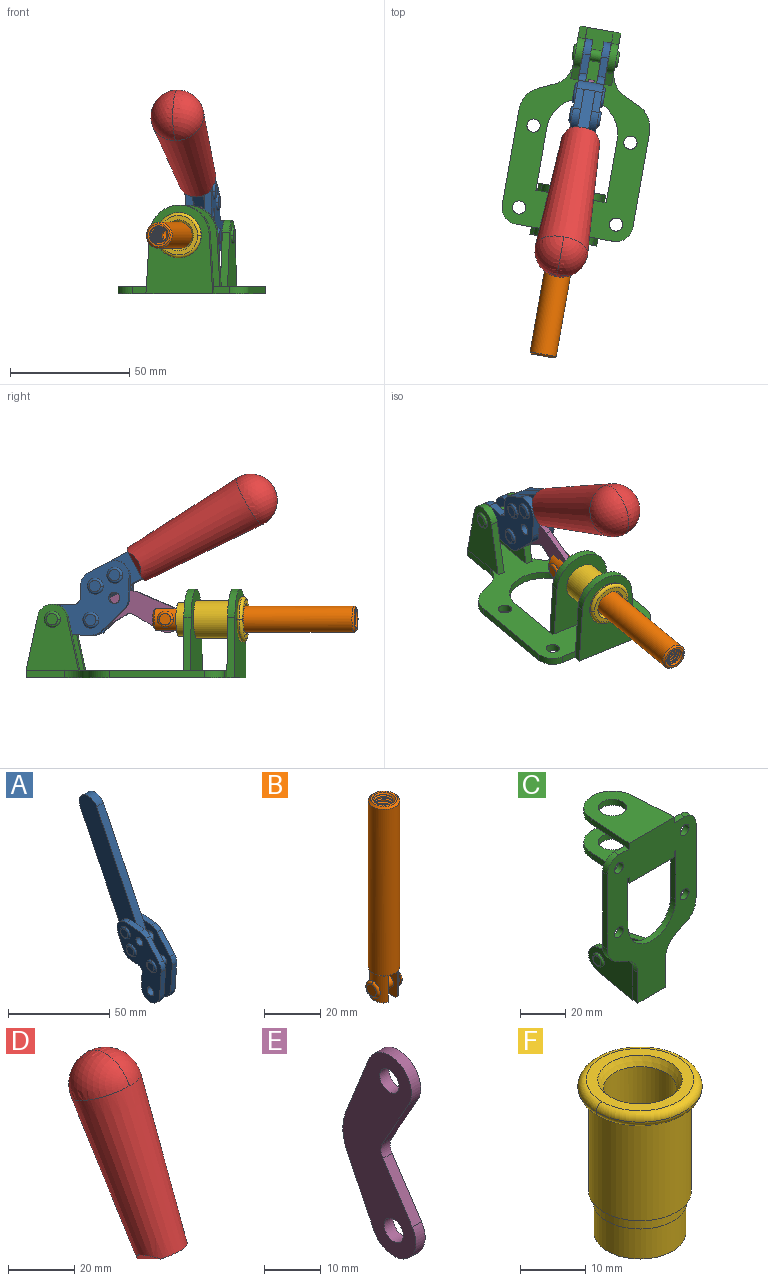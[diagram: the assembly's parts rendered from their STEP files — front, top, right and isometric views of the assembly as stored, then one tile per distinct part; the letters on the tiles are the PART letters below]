
ASSEMBLY  parts=6 mates=6
PART A: 59 faces, bbox 12.9x60.2x99.6 mm
  f0: torus R=2.39mm, axis (-1,0,0), area 14.9mm2, adj f20,f43,f51
  f1: torus R=2.39mm, axis (-1,0,0), area 14.9mm2, adj f19,f42,f51
  f2: torus R=2.39mm, axis (-1,0,0), area 14.9mm2, adj f18,f35,f51
  f3: torus R=2.39mm, axis (-1,0,0), area 14.9mm2, adj f14,f17,f23
  f4: torus R=2.39mm, axis (-1,0,0), area 14.9mm2, adj f13,f16,f23
  f5: torus R=2.39mm, axis (-1,0,0), area 14.9mm2, adj f12,f15,f23
  f6: cylinder r=2.39mm len=4.78mm, axis (1,0,0), area 46.5mm2, adj f48,f50,f51
  f7: cylinder r=2.39mm len=4.78mm, axis (1,0,0), area 46.5mm2, adj f50,f51
  f8: cylinder r=6.35mm len=12.68mm, axis (1,0,0), area 61.8mm2, adj f38,f39,f50,f51
  f9: cylinder r=2.39mm len=4.78mm, axis (-1,0,0), area 70.5mm2, adj f46,f50
  f10: cylinder r=2.39mm len=4.78mm, axis (-1,0,0), area 46.5mm2, adj f23,f45,f46
  f11: cylinder r=2.39mm len=4.78mm, axis (-1,0,0), area 46.5mm2, adj f23,f46
  f12: plane 4.78x4.78mm, normal (1,0,0), area 17.9mm2, adj f5,f15
  f13: plane 4.78x4.78mm, normal (1,0,0), area 17.9mm2, adj f4,f16
  f14: plane 4.78x4.78mm, normal (1,0,0), area 17.9mm2, adj f3,f17
  f15: torus R=2.39mm, axis (-1,0,0), area 14.9mm2, adj f5,f12,f23
  f16: torus R=2.39mm, axis (-1,0,0), area 14.9mm2, adj f4,f13,f23
  f17: torus R=2.39mm, axis (-1,0,0), area 14.9mm2, adj f3,f14,f23
  f18: plane 4.78x4.78mm, normal (-1,0,0), area 17.9mm2, adj f2,f35
  f19: plane 4.78x4.78mm, normal (-1,0,0), area 17.9mm2, adj f1,f42
  f20: plane 4.78x4.78mm, normal (-1,0,0), area 17.9mm2, adj f0,f43
  f21: plane 2.26x0.2mm, normal (1,0,0), area 0.2mm2, adj f31,f44
  f22: plane 2.26x0.2mm, normal (-1,0,0), area 0.2mm2, adj f41,f44
  f23: plane 39.37x30.77mm, normal (1,0,0), area 565.5mm2, adj f3,f4,f5,f10,f11,f15,f16,f17
  f24: cylinder r=6.1mm len=4.15mm, axis (-1,0,0), area 14.7mm2, adj f23,f25,f32,f46
  f25: plane 10.25x9.01mm, normal (0,-0.75,0.66), area 42.3mm2, adj f23,f24,f26,f46
  f26: cylinder r=6.35mm len=4.64mm, axis (-1,0,0), area 15.6mm2, adj f23,f25,f27,f46
  f27: plane 15.84x3.1mm, normal (0,-1,-0.07), area 49.2mm2, adj f23,f26,f28,f46
  f28: cylinder r=6.35mm len=12.68mm, axis (-1,0,0), area 61.8mm2, adj f23,f27,f29,f46
  f29: plane 8.11x3.1mm, normal (0,1,0.07), area 25.2mm2, adj f23,f28,f30,f46
  f30: cylinder r=3.05mm len=3.25mm, axis (-1,0,0), area 14.8mm2, adj f23,f29,f31,f46
  f31: plane 5.99x3.1mm, normal (0,0.07,-1), area 18.6mm2, adj f21,f23,f30,f44,f46
  f32: plane 9.5x3.1mm, normal (0,-0.07,1), area 29.5mm2, adj f23,f24,f33,f46,f47
  f33: cylinder r=6.1mm len=8.63mm, axis (-1,0,0), area 39.1mm2, adj f23,f32,f34,f47
  f34: plane 8.65x3.96mm, normal (0,0.91,-0.42), area 29.5mm2, adj f23,f33,f44,f47
  f35: torus R=2.39mm, axis (-1,0,0), area 14.9mm2, adj f2,f18,f51
  f36: plane 10.25x9.01mm, normal (0,-0.75,0.66), area 42.3mm2, adj f37,f49,f50,f51
  f37: cylinder r=6.35mm len=4.64mm, axis (1,0,0), area 15.6mm2, adj f36,f38,f50,f51
  f38: plane 15.84x3.1mm, normal (0,-1,-0.07), area 49.2mm2, adj f8,f37,f50,f51
  f39: plane 8.11x3.1mm, normal (0,1,0.07), area 25.2mm2, adj f8,f40,f50,f51
  f40: cylinder r=3.05mm len=3.25mm, axis (1,0,0), area 14.8mm2, adj f39,f41,f50,f51
  f41: plane 5.99x3.1mm, normal (0,0.07,-1), area 18.6mm2, adj f22,f40,f44,f50,f51
  f42: torus R=2.39mm, axis (-1,0,0), area 14.9mm2, adj f1,f19,f51
  f43: torus R=2.39mm, axis (-1,0,0), area 14.9mm2, adj f0,f20,f51
  f44: cylinder r=6.35mm len=12.12mm, axis (-1,0,0), area 128.9mm2, adj f21,f22,f23,f31,f34,f41,f46,f47
  f45: plane 2.65x1.35mm, normal (1,0,0), area 1mm2, adj f10,f55
  f46: plane 39.08x20.42mm, normal (-1,0,0), area 412.5mm2, adj f9,f10,f11,f24,f25,f26,f27,f28
  f47: plane 77.62x39.82mm, normal (1,0,0), area 850mm2, adj f32,f33,f34,f44,f53,f54,f55
  f48: plane 2.65x1.35mm, normal (-1,0,0), area 1mm2, adj f6,f55
  f49: cylinder r=6.1mm len=4.15mm, axis (1,0,0), area 14.7mm2, adj f36,f50,f51,f56
  f50: plane 39.08x20.42mm, normal (1,0,0), area 412.5mm2, adj f6,f7,f8,f9,f36,f37,f38,f39
  f51: plane 39.37x30.77mm, normal (-1,0,0), area 565.5mm2, adj f0,f1,f2,f6,f7,f8,f35,f36
  f52: plane 8.65x3.96mm, normal (0,0.91,-0.42), area 29.5mm2, adj f44,f51,f57,f58
  f53: plane 68.49x33.4mm, normal (0,0.9,-0.44), area 358.1mm2, adj f44,f47,f54,f58
  f54: cylinder r=6.35mm len=12.06mm, axis (1,0,0), area 93.7mm2, adj f47,f53,f55,f58
  f55: plane 68.49x33.4mm, normal (0,-0.9,0.44), area 358.1mm2, adj f44,f45,f46,f47,f48,f50,f54,f58
  f56: plane 9.5x3.1mm, normal (0,-0.07,1), area 29.5mm2, adj f49,f50,f51,f57,f58
  f57: cylinder r=6.1mm len=8.63mm, axis (1,0,0), area 39.1mm2, adj f51,f52,f56,f58
  f58: plane 77.62x39.82mm, normal (-1,0,0), area 850mm2, adj f44,f52,f53,f54,f55,f56,f57
PART B: 48 faces, bbox 12.6x11.1x86.1 mm
  f0: torus R=2.41mm, axis (-1,0,0), area 15mm2, adj f30,f32,f34
  f1: torus R=2.41mm, axis (-1,0,0), area 15mm2, adj f29,f31,f33
  f2: cylinder r=5.54mm len=72.39mm, axis (0,0,1), area 2518.5mm2, adj f3,f4,f42,f43
  f3: cone r=5.54mm half-angle=45deg, axis (0,0,1), area 7.6mm2, adj f2,f5,f41
  f4: cone r=5.54mm half-angle=45deg, axis (0,0,-1), area 34.9mm2, adj f2,f39
  f5: cylinder r=5.08mm len=11.48mm, axis (0,0,1), area 108.3mm2, adj f3,f7,f8,f41
  f6: cylinder r=2.41mm len=4.83mm, axis (-1,0,0), area 71.2mm2, adj f40,f41
  f7: cylinder r=2.41mm len=4.83mm, axis (-1,0,0), area 7.6mm2, adj f5,f34
  f8: cone r=5.08mm half-angle=45deg, axis (0,0,1), area 10.6mm2, adj f5,f37,f41
  f9: cone r=3.98mm half-angle=45deg, axis (0,0,1), area 17.6mm2, adj f27,f39,f45,f46,f47
  f10: cylinder r=2.41mm len=4.83mm, axis (-1,0,0), area 7.6mm2, adj f33,f38
  f11: cylinder r=3.2mm len=6.4mm, axis (0,0,1), area 78.4mm2, adj f12,f28,f44,f45,f47
  f12: cylinder r=3.2mm len=6.4mm, axis (0,0,1), area 10.5mm2, adj f11,f13,f45,f47
  f13: cylinder r=3.2mm len=6.4mm, axis (0,0,1), area 10.5mm2, adj f12,f14,f45,f47
  f14: cylinder r=3.2mm len=6.4mm, axis (0,0,1), area 10.5mm2, adj f13,f15,f45,f47
  f15: cylinder r=3.2mm len=6.4mm, axis (0,0,1), area 10.5mm2, adj f14,f16,f45,f47
  f16: cylinder r=3.2mm len=6.4mm, axis (0,0,1), area 10.5mm2, adj f15,f17,f45,f47
  f17: cylinder r=3.2mm len=6.4mm, axis (0,0,1), area 10.5mm2, adj f16,f18,f45,f47
  f18: cylinder r=3.2mm len=6.4mm, axis (0,0,1), area 10.5mm2, adj f17,f19,f45,f47
  f19: cylinder r=3.2mm len=6.4mm, axis (0,0,1), area 10.5mm2, adj f18,f20,f45,f47
  f20: cylinder r=3.2mm len=6.4mm, axis (0,0,1), area 10.5mm2, adj f19,f21,f45,f47
  f21: cylinder r=3.2mm len=6.4mm, axis (0,0,1), area 10.5mm2, adj f20,f22,f45,f47
  f22: cylinder r=3.2mm len=6.4mm, axis (0,0,1), area 10.5mm2, adj f21,f23,f45,f47
  f23: cylinder r=3.2mm len=6.4mm, axis (0,0,1), area 10.5mm2, adj f22,f24,f45,f47
  f24: cylinder r=3.2mm len=6.4mm, axis (0,0,1), area 10.5mm2, adj f23,f25,f45,f47
  f25: cylinder r=3.2mm len=6.4mm, axis (0,0,1), area 10.5mm2, adj f24,f26,f45,f47
  f26: cylinder r=3.2mm len=6.4mm, axis (0,0,1), area 10.5mm2, adj f25,f27,f45,f47
  f27: cylinder r=3.2mm len=6.4mm, axis (0,0,1), area 7.4mm2, adj f9,f26,f45,f47
  f28: cone r=3.2mm half-angle=60deg, axis (0,0,1), area 37.2mm2, adj f11
  f29: plane 4.83x4.83mm, normal (-1,0,0), area 18.3mm2, adj f1,f31
  f30: plane 4.83x4.83mm, normal (1,0,0), area 18.3mm2, adj f0,f32
  f31: torus R=2.41mm, axis (-1,0,0), area 15mm2, adj f1,f29,f33
  f32: torus R=2.41mm, axis (-1,0,0), area 15mm2, adj f0,f30,f34
  f33: plane 6.83x6.83mm, normal (1,0,0), area 18.3mm2, adj f1,f10,f31
  f34: plane 6.83x6.83mm, normal (-1,0,0), area 18.3mm2, adj f0,f7,f32
  f35: cone r=5.08mm half-angle=45deg, axis (0,0,1), area 10.6mm2, adj f36,f38,f40
  f36: plane 7.25x1.97mm, normal (0,0,-1), area 10mm2, adj f35,f40
  f37: plane 7.25x1.97mm, normal (0,0,-1), area 10mm2, adj f8,f41
  f38: cylinder r=5.08mm len=11.48mm, axis (0,0,1), area 108.3mm2, adj f10,f35,f40,f42
  f39: plane 9.55x9.55mm, normal (0,0,1), area 22mm2, adj f4,f9
  f40: plane 12.76x10.09mm, normal (1,0,0), area 95.7mm2, adj f6,f35,f36,f38,f42,f43
  f41: plane 12.76x10.09mm, normal (-1,0,0), area 95.7mm2, adj f3,f5,f6,f8,f37,f43
  f42: cone r=5.54mm half-angle=45deg, axis (0,0,1), area 7.6mm2, adj f2,f38,f40
  f43: plane 11.07x4.7mm, normal (0,0,-1), area 50.4mm2, adj f2,f40,f41
  f44: plane 0.89x0.62mm, normal (-1,0,0), area 0.3mm2, adj f11,f45,f46,f47
  f45: bspline ~24.8x7.63mm, area 266.6mm2, adj f9,f11,f12,f13,f14,f15,f16,f17
  f46: bspline ~24.87x7.63mm, area 73.6mm2, adj f9,f44,f45,f47
  f47: bspline ~24.98x7.63mm, area 272.5mm2, adj f9,f11,f12,f13,f14,f15,f16,f17
PART C: 55 faces, bbox 55.7x37.4x89.8 mm
  f0: torus R=2.41mm, axis (-1,0,0), area 15mm2, adj f11,f15,f25
  f1: torus R=2.41mm, axis (-1,0,0), area 15mm2, adj f10,f12,f22
  f2: cylinder r=2.78mm len=5.56mm, axis (0,-1,0), area 54.2mm2, adj f30,f54
  f3: cylinder r=14.99mm len=29.97mm, axis (0,-1,0), area 145.9mm2, adj f30,f49,f53,f54
  f4: cylinder r=2.78mm len=5.56mm, axis (0,-1,0), area 54.2mm2, adj f30,f54
  f5: cylinder r=2.78mm len=5.56mm, axis (0,-1,0), area 54.2mm2, adj f30,f54
  f6: cylinder r=2.78mm len=5.56mm, axis (0,-1,0), area 54.2mm2, adj f30,f54
  f7: cylinder r=6.35mm len=12.7mm, axis (0,0,1), area 123.6mm2, adj f27,f51
  f8: cylinder r=6.35mm len=12.7mm, axis (0,0,-1), area 124.7mm2, adj f21,f35
  f9: cylinder r=2.41mm len=11.18mm, axis (-1,0,0), area 169.4mm2, adj f16,f19
  f10: plane 4.83x4.83mm, normal (1,0,0), area 18.3mm2, adj f1,f12
  f11: plane 4.83x4.83mm, normal (-1,0,0), area 18.3mm2, adj f0,f15
  f12: torus R=2.41mm, axis (-1,0,0), area 15mm2, adj f1,f10,f22
  f13: cylinder r=6.35mm len=12.41mm, axis (1,0,0), area 53.4mm2, adj f18,f19,f22,f23
  f14: cylinder r=6.35mm len=12.41mm, axis (-1,0,0), area 53.4mm2, adj f16,f17,f24,f25
  f15: torus R=2.41mm, axis (-1,0,0), area 15mm2, adj f0,f11,f25
  f16: plane 27.86x22.35mm, normal (1,0,0), area 425.4mm2, adj f9,f14,f17,f24,f30
  f17: plane 22.86x4.97mm, normal (0,0.21,0.98), area 72.5mm2, adj f14,f16,f25,f30
  f18: plane 22.86x4.97mm, normal (0,0.21,0.98), area 72.5mm2, adj f13,f19,f22,f30
  f19: plane 27.86x22.35mm, normal (-1,0,0), area 425.4mm2, adj f9,f13,f18,f23,f30
  f20: cylinder r=12.7mm len=25.35mm, axis (0,0,-1), area 119.8mm2, adj f21,f34,f35,f36
  f21: plane 34.21x28.07mm, normal (0,0,-1), area 702.4mm2, adj f8,f20,f30,f34,f36
  f22: plane 27.96x22.45mm, normal (1,0,0), area 407.2mm2, adj f1,f12,f13,f18,f23,f30,f42,f43
  f23: plane 22.86x4.97mm, normal (0,0.21,-0.98), area 72.5mm2, adj f13,f19,f22,f44
  f24: plane 22.86x4.97mm, normal (0,0.21,-0.98), area 72.5mm2, adj f14,f16,f25,f44
  f25: plane 27.86x22.35mm, normal (-1,0,0), area 407.1mm2, adj f0,f14,f15,f17,f24,f30,f45,f46
  f26: plane 3.1x0.95mm, normal (0,0,-1), area 2.7mm2, adj f30,f49,f50,f54
  f27: plane 34.21x28.07mm, normal (0,0,1), area 702.4mm2, adj f7,f28,f30,f50,f52
  f28: cylinder r=12.7mm len=25.35mm, axis (0,0,1), area 118.8mm2, adj f27,f50,f51,f52
  f29: plane 3.1x0.95mm, normal (0,0,-1), area 2.7mm2, adj f30,f52,f53,f54
  f30: plane 86.54x55.63mm, normal (0,1,0), area 2362.9mm2, adj f2,f3,f4,f5,f6,f16,f17,f18
  f31: plane 40.56x3.1mm, normal (-1,0,0), area 125.7mm2, adj f30,f32,f48,f54
  f32: cylinder r=7.11mm len=7.11mm, axis (0,-1,0), area 34.6mm2, adj f30,f31,f33,f54
  f33: plane 6.67x3.1mm, normal (0,0,1), area 20.4mm2, adj f30,f32,f34,f54
  f34: plane 25.39x3.13mm, normal (-1,0.06,0), area 79.5mm2, adj f20,f21,f33,f35,f54
  f35: plane 37.31x28.45mm, normal (0,0,1), area 789.9mm2, adj f8,f20,f34,f36,f54
  f36: plane 25.39x3.13mm, normal (1,0.06,0), area 79.5mm2, adj f20,f21,f35,f37,f54
  f37: plane 6.67x3.1mm, normal (0,0,1), area 20.4mm2, adj f30,f36,f38,f54
  f38: cylinder r=7.11mm len=7.11mm, axis (0,-1,0), area 34.6mm2, adj f30,f37,f39,f54
  f39: plane 40.56x3.1mm, normal (1,0,0), area 125.7mm2, adj f30,f38,f40,f54
  f40: cylinder r=11.18mm len=10.16mm, axis (0,-1,0), area 39.5mm2, adj f30,f39,f41,f54
  f41: plane 6.09x3.1mm, normal (0.42,0,-0.91), area 20.8mm2, adj f30,f40,f42,f54
  f42: cylinder r=11.18mm len=9.41mm, axis (0,-1,0), area 37.2mm2, adj f22,f30,f41,f43,f54
  f43: plane 16.5x3.1mm, normal (1,0,0), area 51.1mm2, adj f22,f42,f44,f54
  f44: plane 17.37x3.1mm, normal (0,0,-1), area 53.8mm2, adj f23,f24,f30,f43,f45,f54
  f45: plane 16.5x3.1mm, normal (-1,0,0), area 51.1mm2, adj f25,f44,f46,f54
  f46: cylinder r=11.18mm len=9.41mm, axis (0,-1,0), area 37.2mm2, adj f25,f30,f45,f47,f54
  f47: plane 6.09x3.1mm, normal (-0.42,0,-0.91), area 20.8mm2, adj f30,f46,f48,f54
  f48: cylinder r=11.18mm len=10.16mm, axis (0,-1,0), area 39.5mm2, adj f30,f31,f47,f54
  f49: plane 26.54x3.1mm, normal (-1,0,0), area 82.3mm2, adj f3,f26,f30,f54
  f50: plane 25.39x3.1mm, normal (1,0.06,0), area 78.8mm2, adj f26,f27,f28,f51,f54
  f51: plane 37.31x28.45mm, normal (0,0,-1), area 789.9mm2, adj f7,f28,f50,f52,f54
  f52: plane 25.39x3.1mm, normal (-1,0.06,0), area 78.8mm2, adj f27,f28,f29,f51,f54
  f53: plane 26.54x3.1mm, normal (1,0,0), area 82.3mm2, adj f3,f29,f30,f54
  f54: plane 89.66x55.63mm, normal (0,-1,0), area 2678.5mm2, adj f2,f3,f4,f5,f6,f26,f29,f31
PART D: 11 faces, bbox 22.3x42.6x64.5 mm
  f0: sphere r=11.13mm, area 411.4mm2, adj f1,f8
  f1: cone r=11.11mm half-angle=3.3deg, axis (0,0.44,0.9), area 3251.8mm2, adj f0,f7,f8,f9,f10
  f2: cylinder r=6.16mm len=11.7mm, axis (1,0,0), area 89.5mm2, adj f3,f4,f5,f6
  f3: plane 60.23x36.75mm, normal (-1,0,0), area 763.6mm2, adj f2,f4,f6,f10
  f4: plane 51.37x25.05mm, normal (0,0.9,-0.44), area 264.2mm2, adj f2,f3,f5,f10
  f5: plane 60.23x36.75mm, normal (1,0,0), area 763.6mm2, adj f2,f4,f6,f10
  f6: plane 51.37x25.05mm, normal (0,-0.9,0.44), area 264.2mm2, adj f2,f3,f5,f10
  f7: plane 9.95x5.95mm, normal (0.71,-0.31,-0.64), area 25.8mm2, adj f1,f10
  f8: sphere r=11.13mm, area 411.4mm2, adj f0,f1
  f9: plane 9.95x5.95mm, normal (-0.71,-0.31,-0.64), area 25.8mm2, adj f1,f10
  f10: plane 14.27x11.38mm, normal (0,-0.44,-0.9), area 106.7mm2, adj f1,f3,f4,f5,f6,f7,f9
PART E: 12 faces, bbox 2.3x18.2x42.8 mm
  f0: cylinder r=2.4mm len=4.8mm, axis (1,0,0), area 34.9mm2, adj f4,f11
  f1: cylinder r=10.41mm len=8.47mm, axis (1,0,0), area 20.2mm2, adj f4,f9,f10,f11
  f2: cylinder r=3.05mm len=3.16mm, axis (1,0,0), area 7.7mm2, adj f4,f6,f7,f11
  f3: cylinder r=2.4mm len=4.8mm, axis (1,0,0), area 34.9mm2, adj f4,f11
  f4: plane 42.81x18.23mm, normal (-1,0,0), area 414.1mm2, adj f0,f1,f2,f3,f5,f6,f7,f8
  f5: cylinder r=5.54mm len=10.67mm, axis (1,0,0), area 41.8mm2, adj f4,f6,f10,f11
  f6: plane 11.66x6.53mm, normal (0,-0.87,-0.49), area 30.9mm2, adj f2,f4,f5,f11
  f7: plane 11.17x7.33mm, normal (0,-0.84,0.55), area 30.9mm2, adj f2,f4,f8,f11
  f8: cylinder r=5.54mm len=10.51mm, axis (1,0,0), area 41.8mm2, adj f4,f7,f9,f11
  f9: plane 13.67x6.67mm, normal (0,0.9,-0.44), area 35.1mm2, adj f1,f4,f8,f11
  f10: plane 14.1x5.7mm, normal (0,0.93,0.37), area 35.1mm2, adj f1,f4,f5,f11
  f11: plane 42.81x18.23mm, normal (1,0,0), area 414.1mm2, adj f0,f1,f2,f3,f5,f6,f7,f8
PART F: 15 faces, bbox 20.6x20.6x28.7 mm
  f0: torus R=8.26mm, axis (0,0,1), area 56.8mm2, adj f1,f10,f12
  f1: torus R=8.26mm, axis (0,0,1), area 56.8mm2, adj f0,f6,f13
  f2: cylinder r=5.59mm len=25.91mm, axis (0,0,1), area 909.6mm2, adj f3,f4
  f3: cone r=6.86mm half-angle=45deg, axis (0,0,-1), area 70.2mm2, adj f2,f14
  f4: cone r=6.47mm half-angle=30deg, axis (0,0,1), area 66.7mm2, adj f2,f13
  f5: cylinder r=7.04mm len=14.07mm, axis (0,0,1), area 252.6mm2, adj f11,f14
  f6: torus R=8.26mm, axis (0,0,1), area 56.8mm2, adj f1,f12,f13
  f7: cylinder r=7.16mm len=14.33mm, axis (0,0,1), area 91.5mm2, adj f9,f11
  f8: cylinder r=7.86mm len=18.42mm, axis (0,0,1), area 909.6mm2, adj f9,f10
  f9: plane 15.72x15.72mm, normal (0,0,-1), area 33mm2, adj f7,f8
  f10: plane 16.51x16.51mm, normal (0,0,-1), area 19.9mm2, adj f0,f8,f12
  f11: plane 14.33x14.33mm, normal (0,0,-1), area 5.7mm2, adj f5,f7
  f12: torus R=8.26mm, axis (0,0,1), area 56.8mm2, adj f0,f6,f10
  f13: plane 16.51x16.51mm, normal (0,0,1), area 82.7mm2, adj f1,f4,f6
  f14: plane 14.07x14.07mm, normal (0,0,-1), area 7.8mm2, adj f3,f5
PLACE A rot(axis=(0.99,-0.09,-0.09),87.7deg) t=(-0.2,-1.13,1.58)mm
PLACE B rot(axis=(0.99,-0.09,-0.09),90.4deg) t=(-0.01,-0.05,0)mm
PLACE C rot(axis=(0.99,-0.09,-0.09),90.4deg) t=(0,0,0)mm fixed
PLACE D rot(axis=(0.99,-0.09,-0.09),87.7deg) t=(-0.2,-1.13,1.58)mm
PLACE E rot(axis=(0.06,0.72,0.69),173.1deg) t=(-0.06,-0.35,0.39)mm
PLACE F rot(axis=(0.99,-0.09,-0.09),90.4deg) t=(0,0,0)mm
MATE slider B.f2 <-> C.f7  axis (-0.17,-0.98,0) through (-10.22,-57.94,24.61)mm
MATE revolute E.f5 <-> A.f4  axis (-0.98,0.17,0) through (2.82,15.98,24.27)mm
MATE fastened A.f54 <-> D.f2  axis (0.98,-0.17,0) through (-9.1,-51.63,75.18)mm
MATE revolute C.f0 <-> A.f7  axis (-0.98,0.17,0) through (5.57,31.61,24.61)mm
MATE revolute B.f6 <-> E.f3  axis (-0.98,0.17,0) through (-2.7,-15.29,24.61)mm
MATE fastened F.f2 <-> C.f7  axis (0.17,0.98,0) through (-8.06,-45.69,24.61)mm
